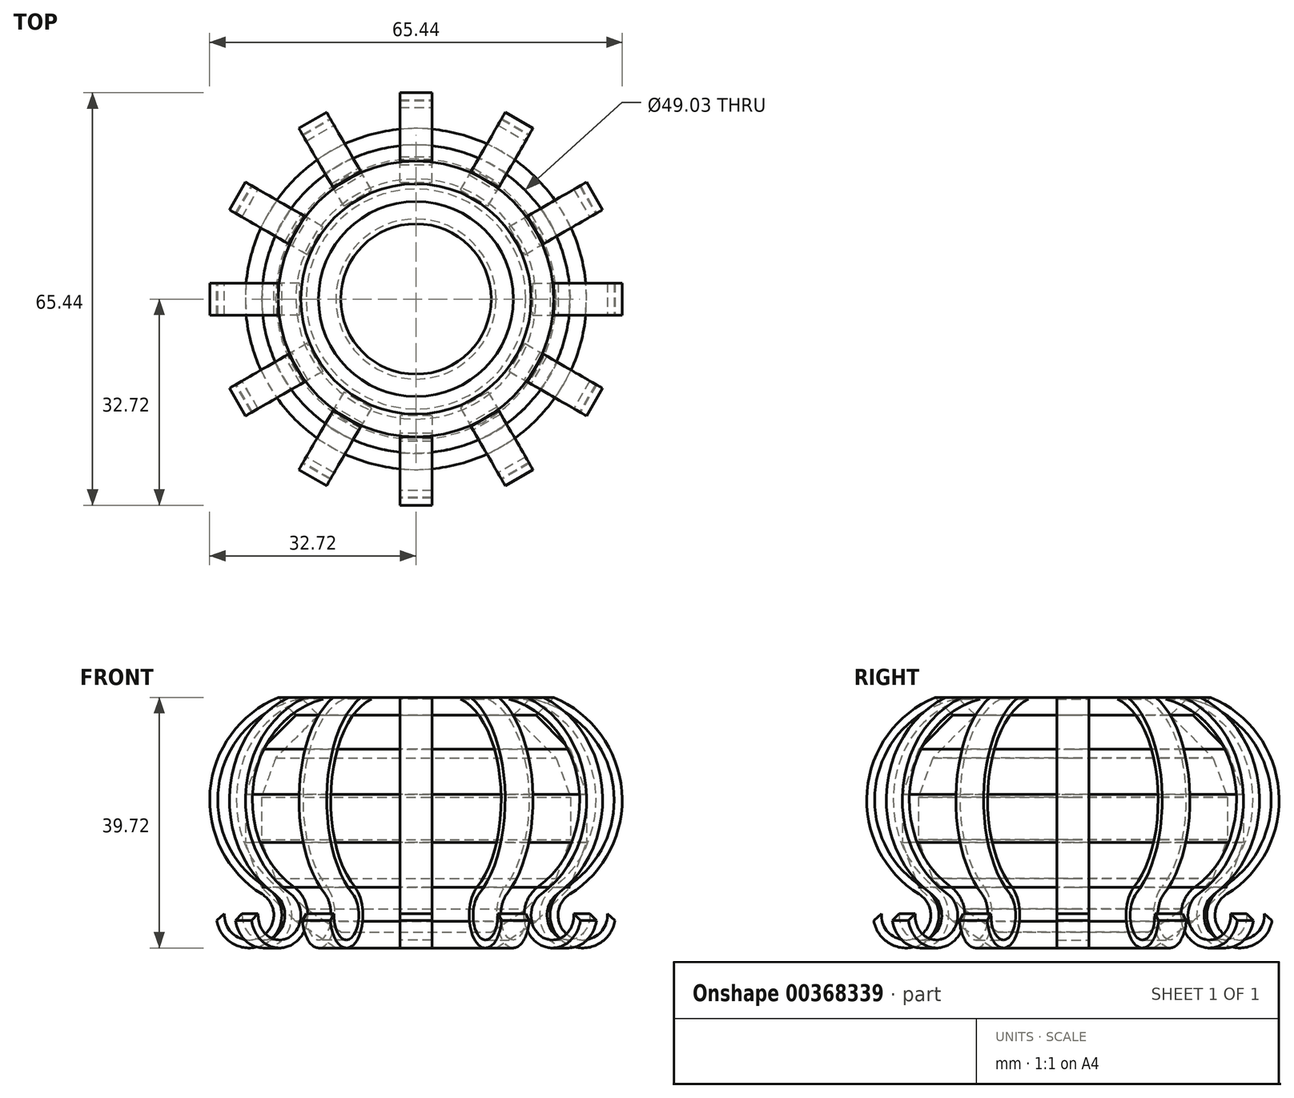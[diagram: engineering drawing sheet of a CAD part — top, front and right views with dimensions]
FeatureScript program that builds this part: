
annotation { "Feature Type Name" : "Feature", "Feature Type Description" : "" }
export const myFeature = defineFeature(function(context is Context, id is Id, definition is map)
    precondition{}
    {
        {
            var Q0;
            Q0=qCreatedBy(makeId("Front.planeOp"),FACE);
            var sketch = newSketch(context, id + "F0", { "sketchPlane" : qUnion([Q0])});
            skLineSegment(sketch, "E0", {"start": v(0, -23.47) * mm, "end": v(-12.7, -23.47) * mm});
            skLineSegment(sketch, "E1", {"start": v(-12.7, -23.47) * mm, "end": v(-19.05, -19.26) * mm});
            skLineSegment(sketch, "E2", {"start": v(-19.05, -19.26) * mm, "end": v(-24.44, -13.87) * mm});
            skLineSegment(sketch, "E3", {"start": v(-24.44, -13.87) * mm, "end": v(-27.06, -6.72) * mm});
            skLineSegment(sketch, "E4", {"start": v(-27.06, -6.72) * mm, "end": v(-27.06, 0.9) * mm});
            skLineSegment(sketch, "E5", {"start": v(-27.06, 0.9) * mm, "end": v(-24.44, 8.06) * mm});
            skLineSegment(sketch, "E6", {"start": v(-24.44, 8.06) * mm, "end": v(-19.05, 13.45) * mm});
            skLineSegment(sketch, "E7", {"start": v(-19.05, 13.45) * mm, "end": v(-21.86, 16.25) * mm});
            skLineSegment(sketch, "E8.0", {"start": v(-15.46, 13.45) * mm, "end": v(-18.27, 16.25) * mm});
            skLineSegment(sketch, "E8.1", {"start": v(-22.25, 6.66) * mm, "end": v(-15.46, 13.45) * mm});
            skLineSegment(sketch, "E8.2", {"start": v(-24.52, 0.45) * mm, "end": v(-22.25, 6.66) * mm});
            skLineSegment(sketch, "E8.3", {"start": v(-24.52, -6.27) * mm, "end": v(-24.52, 0.45) * mm});
            skLineSegment(sketch, "E8.4", {"start": v(0, -20.93) * mm, "end": v(-11.93, -20.93) * mm});
            skLineSegment(sketch, "E8.5", {"start": v(-11.93, -20.93) * mm, "end": v(-17.43, -17.28) * mm});
            skLineSegment(sketch, "E8.6", {"start": v(-17.43, -17.28) * mm, "end": v(-22.25, -12.47) * mm});
            skLineSegment(sketch, "E8.7", {"start": v(-22.25, -12.47) * mm, "end": v(-24.52, -6.27) * mm});
            skLineSegment(sketch, "E9", {"start": v(-21.86, 16.25) * mm, "end": v(-18.27, 16.25) * mm});
            skLineSegment(sketch, "E10", {"start": v(0, -23.47) * mm, "end": v(0, -20.93) * mm});
            skSolve(sketch);
        }
        {
            var Q0;
            Q0 = qSketchRegion(id + "F0", true);
            var Q1;
            Q1=sQuery(id+"F0.wireOp",EDGE,"E10");
            revolve(context, id + "F1", {"entities" : qUnion([Q0]), "axis" : qUnion([Q1]), "revolveType" : RevolveType.FULL});
        }
        {
            var Q0;
            Q0=qCreatedBy(makeId("Front.planeOp"),FACE);
            var sketch = newSketch(context, id + "F2", { "sketchPlane" : qUnion([Q0])});
            skArc(sketch, "E11", {"start": v(-21.86, 16.25) * mm, "mid": v(-32.66, 1.43) * mm, "end": v(-24.4, -14.95) * mm});
            skArc(sketch, "E12", {"start": v(-30.38, -18.03) * mm, "mid": v(-24.67, -21.77) * mm, "end": v(-24.4, -14.95) * mm});
            skLineSegment(sketch, "E13", {"start": v(-29.58, -23.47) * mm, "end": v(-12.7, -23.47) * mm, "construction": true});
            skArc(sketch, "E14.0", {"start": v(-31.59, -19.1) * mm, "mid": v(-23.59, -22.6) * mm, "end": v(-23.73, -13.87) * mm});
            skArc(sketch, "E14.1", {"start": v(-18.5, 15.97) * mm, "mid": v(-31.2, 2.82) * mm, "end": v(-23.73, -13.87) * mm});
            skLineSegment(sketch, "E15", {"start": v(-31.59, -19.1) * mm, "end": v(-30.38, -18.03) * mm});
            skLineSegment(sketch, "E16", {"start": v(-18.5, 15.97) * mm, "end": v(-21.86, 16.25) * mm});
            skSolve(sketch);
        }
        {
            var Q0;
            Q0 = qSketchRegion(id + "F2", true);
            extrude(context, id + "F3", {"entities" : qUnion([Q0]), "endBound" : BoundingType.SYMMETRIC, "depth" : 5.08 * mm});
        }
        {
            var Q0;
            Q0=makeQuery(id+"F3.opExtrude","SWEPT_BODY",BODY,{"disambiguationData":[OSD([sQuery(id+"F2.wireOp",EDGE,"E11"),sQuery(id+"F2.wireOp",EDGE,"E12"),sQuery(id+"F2.wireOp",EDGE,"E14.0"),sQuery(id+"F2.wireOp",EDGE,"E14.1"),sQuery(id+"F2.wireOp",EDGE,"E15"),sQuery(id+"F2.wireOp",EDGE,"E16")])]});
            var Q1;
            Q1=sQuery(id+"F0.wireOp",EDGE,"E10");
            transform(context, id + "F4", {"entities" : qUnion([Q0]), "transformType" : TransformType.ROTATION, "transformAxis" : qUnion([Q1]), "angle" : 30 * degree, "makeCopy" : true});
        }
        {
            var Q0;
            Q0=makeQuery(id+"F4.opPattern","COPY",BODY,{"derivedFrom":makeQuery(id+"F3.opExtrude","SWEPT_BODY",BODY,{"disambiguationData":[OSD([sQuery(id+"F2.wireOp",EDGE,"E11"),sQuery(id+"F2.wireOp",EDGE,"E12"),sQuery(id+"F2.wireOp",EDGE,"E14.0"),sQuery(id+"F2.wireOp",EDGE,"E14.1"),sQuery(id+"F2.wireOp",EDGE,"E15"),sQuery(id+"F2.wireOp",EDGE,"E16")])]}),"instanceName":"1"});
            var Q1;
            Q1=sQuery(id+"F0.wireOp",EDGE,"E10");
            transform(context, id + "F5", {"entities" : qUnion([Q0]), "transformType" : TransformType.ROTATION, "transformAxis" : qUnion([Q1]), "angle" : 30 * degree, "makeCopy" : true});
        }
        {
            var Q0;
            Q0=makeQuery(id+"F5.opPattern","COPY",BODY,{"derivedFrom":makeQuery(id+"F4.opPattern","COPY",BODY,{"derivedFrom":makeQuery(id+"F3.opExtrude","SWEPT_BODY",BODY,{"disambiguationData":[OSD([sQuery(id+"F2.wireOp",EDGE,"E11"),sQuery(id+"F2.wireOp",EDGE,"E12"),sQuery(id+"F2.wireOp",EDGE,"E14.0"),sQuery(id+"F2.wireOp",EDGE,"E14.1"),sQuery(id+"F2.wireOp",EDGE,"E15"),sQuery(id+"F2.wireOp",EDGE,"E16")])]}),"instanceName":"1"}),"instanceName":"1"});
            var Q1;
            Q1=sQuery(id+"F0.wireOp",EDGE,"E10");
            transform(context, id + "F6", {"entities" : qUnion([Q0]), "transformType" : TransformType.ROTATION, "transformAxis" : qUnion([Q1]), "angle" : 30 * degree, "makeCopy" : true});
        }
        {
            var Q0;
            Q0=makeQuery(id+"F6.opPattern","COPY",BODY,{"derivedFrom":makeQuery(id+"F5.opPattern","COPY",BODY,{"derivedFrom":makeQuery(id+"F4.opPattern","COPY",BODY,{"derivedFrom":makeQuery(id+"F3.opExtrude","SWEPT_BODY",BODY,{"disambiguationData":[OSD([sQuery(id+"F2.wireOp",EDGE,"E11"),sQuery(id+"F2.wireOp",EDGE,"E12"),sQuery(id+"F2.wireOp",EDGE,"E14.0"),sQuery(id+"F2.wireOp",EDGE,"E14.1"),sQuery(id+"F2.wireOp",EDGE,"E15"),sQuery(id+"F2.wireOp",EDGE,"E16")])]}),"instanceName":"1"}),"instanceName":"1"}),"instanceName":"1"});
            var Q1;
            Q1=sQuery(id+"F0.wireOp",EDGE,"E10");
            transform(context, id + "F7", {"entities" : qUnion([Q0]), "transformType" : TransformType.ROTATION, "transformAxis" : qUnion([Q1]), "angle" : 30 * degree, "makeCopy" : true});
        }
        {
            var Q0;
            Q0=makeQuery(id+"F7.opPattern","COPY",BODY,{"derivedFrom":makeQuery(id+"F6.opPattern","COPY",BODY,{"derivedFrom":makeQuery(id+"F5.opPattern","COPY",BODY,{"derivedFrom":makeQuery(id+"F4.opPattern","COPY",BODY,{"derivedFrom":makeQuery(id+"F3.opExtrude","SWEPT_BODY",BODY,{"disambiguationData":[OSD([sQuery(id+"F2.wireOp",EDGE,"E11"),sQuery(id+"F2.wireOp",EDGE,"E12"),sQuery(id+"F2.wireOp",EDGE,"E14.0"),sQuery(id+"F2.wireOp",EDGE,"E14.1"),sQuery(id+"F2.wireOp",EDGE,"E15"),sQuery(id+"F2.wireOp",EDGE,"E16")])]}),"instanceName":"1"}),"instanceName":"1"}),"instanceName":"1"}),"instanceName":"1"});
            var Q1;
            Q1=sQuery(id+"F0.wireOp",EDGE,"E10");
            transform(context, id + "F8", {"entities" : qUnion([Q0]), "transformType" : TransformType.ROTATION, "transformAxis" : qUnion([Q1]), "angle" : 30 * degree, "makeCopy" : true});
        }
        {
            var Q0;
            Q0=makeQuery(id+"F8.opPattern","COPY",BODY,{"derivedFrom":makeQuery(id+"F7.opPattern","COPY",BODY,{"derivedFrom":makeQuery(id+"F6.opPattern","COPY",BODY,{"derivedFrom":makeQuery(id+"F5.opPattern","COPY",BODY,{"derivedFrom":makeQuery(id+"F4.opPattern","COPY",BODY,{"derivedFrom":makeQuery(id+"F3.opExtrude","SWEPT_BODY",BODY,{"disambiguationData":[OSD([sQuery(id+"F2.wireOp",EDGE,"E11"),sQuery(id+"F2.wireOp",EDGE,"E12"),sQuery(id+"F2.wireOp",EDGE,"E14.0"),sQuery(id+"F2.wireOp",EDGE,"E14.1"),sQuery(id+"F2.wireOp",EDGE,"E15"),sQuery(id+"F2.wireOp",EDGE,"E16")])]}),"instanceName":"1"}),"instanceName":"1"}),"instanceName":"1"}),"instanceName":"1"}),"instanceName":"1"});
            var Q1;
            Q1=sQuery(id+"F0.wireOp",EDGE,"E10");
            transform(context, id + "F9", {"entities" : qUnion([Q0]), "transformType" : TransformType.ROTATION, "transformAxis" : qUnion([Q1]), "angle" : 30 * degree, "makeCopy" : true});
        }
        {
            var Q0;
            Q0=makeQuery(id+"F9.opPattern","COPY",BODY,{"derivedFrom":makeQuery(id+"F8.opPattern","COPY",BODY,{"derivedFrom":makeQuery(id+"F7.opPattern","COPY",BODY,{"derivedFrom":makeQuery(id+"F6.opPattern","COPY",BODY,{"derivedFrom":makeQuery(id+"F5.opPattern","COPY",BODY,{"derivedFrom":makeQuery(id+"F4.opPattern","COPY",BODY,{"derivedFrom":makeQuery(id+"F3.opExtrude","SWEPT_BODY",BODY,{"disambiguationData":[OSD([sQuery(id+"F2.wireOp",EDGE,"E11"),sQuery(id+"F2.wireOp",EDGE,"E12"),sQuery(id+"F2.wireOp",EDGE,"E14.0"),sQuery(id+"F2.wireOp",EDGE,"E14.1"),sQuery(id+"F2.wireOp",EDGE,"E15"),sQuery(id+"F2.wireOp",EDGE,"E16")])]}),"instanceName":"1"}),"instanceName":"1"}),"instanceName":"1"}),"instanceName":"1"}),"instanceName":"1"}),"instanceName":"1"});
            var Q1;
            Q1=sQuery(id+"F0.wireOp",EDGE,"E10");
            transform(context, id + "F10", {"entities" : qUnion([Q0]), "transformType" : TransformType.ROTATION, "transformAxis" : qUnion([Q1]), "angle" : 30 * degree, "makeCopy" : true});
        }
        {
            var Q0;
            Q0=makeQuery(id+"F10.opPattern","COPY",BODY,{"derivedFrom":makeQuery(id+"F9.opPattern","COPY",BODY,{"derivedFrom":makeQuery(id+"F8.opPattern","COPY",BODY,{"derivedFrom":makeQuery(id+"F7.opPattern","COPY",BODY,{"derivedFrom":makeQuery(id+"F6.opPattern","COPY",BODY,{"derivedFrom":makeQuery(id+"F5.opPattern","COPY",BODY,{"derivedFrom":makeQuery(id+"F4.opPattern","COPY",BODY,{"derivedFrom":makeQuery(id+"F3.opExtrude","SWEPT_BODY",BODY,{"disambiguationData":[OSD([sQuery(id+"F2.wireOp",EDGE,"E11"),sQuery(id+"F2.wireOp",EDGE,"E12"),sQuery(id+"F2.wireOp",EDGE,"E14.0"),sQuery(id+"F2.wireOp",EDGE,"E14.1"),sQuery(id+"F2.wireOp",EDGE,"E15"),sQuery(id+"F2.wireOp",EDGE,"E16")])]}),"instanceName":"1"}),"instanceName":"1"}),"instanceName":"1"}),"instanceName":"1"}),"instanceName":"1"}),"instanceName":"1"}),"instanceName":"1"});
            var Q1;
            Q1=sQuery(id+"F0.wireOp",EDGE,"E10");
            transform(context, id + "F11", {"entities" : qUnion([Q0]), "transformType" : TransformType.ROTATION, "transformAxis" : qUnion([Q1]), "angle" : 30 * degree, "makeCopy" : true});
        }
        {
            var Q0;
            Q0=makeQuery(id+"F11.opPattern","COPY",BODY,{"derivedFrom":makeQuery(id+"F10.opPattern","COPY",BODY,{"derivedFrom":makeQuery(id+"F9.opPattern","COPY",BODY,{"derivedFrom":makeQuery(id+"F8.opPattern","COPY",BODY,{"derivedFrom":makeQuery(id+"F7.opPattern","COPY",BODY,{"derivedFrom":makeQuery(id+"F6.opPattern","COPY",BODY,{"derivedFrom":makeQuery(id+"F5.opPattern","COPY",BODY,{"derivedFrom":makeQuery(id+"F4.opPattern","COPY",BODY,{"derivedFrom":makeQuery(id+"F3.opExtrude","SWEPT_BODY",BODY,{"disambiguationData":[OSD([sQuery(id+"F2.wireOp",EDGE,"E11"),sQuery(id+"F2.wireOp",EDGE,"E12"),sQuery(id+"F2.wireOp",EDGE,"E14.0"),sQuery(id+"F2.wireOp",EDGE,"E14.1"),sQuery(id+"F2.wireOp",EDGE,"E15"),sQuery(id+"F2.wireOp",EDGE,"E16")])]}),"instanceName":"1"}),"instanceName":"1"}),"instanceName":"1"}),"instanceName":"1"}),"instanceName":"1"}),"instanceName":"1"}),"instanceName":"1"}),"instanceName":"1"});
            var Q1;
            Q1=sQuery(id+"F0.wireOp",EDGE,"E10");
            transform(context, id + "F12", {"entities" : qUnion([Q0]), "transformType" : TransformType.ROTATION, "transformAxis" : qUnion([Q1]), "angle" : 30 * degree, "makeCopy" : true});
        }
        {
            var Q0;
            Q0=makeQuery(id+"F12.opPattern","COPY",BODY,{"derivedFrom":makeQuery(id+"F11.opPattern","COPY",BODY,{"derivedFrom":makeQuery(id+"F10.opPattern","COPY",BODY,{"derivedFrom":makeQuery(id+"F9.opPattern","COPY",BODY,{"derivedFrom":makeQuery(id+"F8.opPattern","COPY",BODY,{"derivedFrom":makeQuery(id+"F7.opPattern","COPY",BODY,{"derivedFrom":makeQuery(id+"F6.opPattern","COPY",BODY,{"derivedFrom":makeQuery(id+"F5.opPattern","COPY",BODY,{"derivedFrom":makeQuery(id+"F4.opPattern","COPY",BODY,{"derivedFrom":makeQuery(id+"F3.opExtrude","SWEPT_BODY",BODY,{"disambiguationData":[OSD([sQuery(id+"F2.wireOp",EDGE,"E11"),sQuery(id+"F2.wireOp",EDGE,"E12"),sQuery(id+"F2.wireOp",EDGE,"E14.0"),sQuery(id+"F2.wireOp",EDGE,"E14.1"),sQuery(id+"F2.wireOp",EDGE,"E15"),sQuery(id+"F2.wireOp",EDGE,"E16")])]}),"instanceName":"1"}),"instanceName":"1"}),"instanceName":"1"}),"instanceName":"1"}),"instanceName":"1"}),"instanceName":"1"}),"instanceName":"1"}),"instanceName":"1"}),"instanceName":"1"});
            var Q1;
            Q1=sQuery(id+"F0.wireOp",EDGE,"E10");
            transform(context, id + "F13", {"entities" : qUnion([Q0]), "transformType" : TransformType.ROTATION, "transformAxis" : qUnion([Q1]), "angle" : 30 * degree, "makeCopy" : true});
        }
        {
            var Q0;
            Q0=makeQuery(id+"F13.opPattern","COPY",BODY,{"derivedFrom":makeQuery(id+"F12.opPattern","COPY",BODY,{"derivedFrom":makeQuery(id+"F11.opPattern","COPY",BODY,{"derivedFrom":makeQuery(id+"F10.opPattern","COPY",BODY,{"derivedFrom":makeQuery(id+"F9.opPattern","COPY",BODY,{"derivedFrom":makeQuery(id+"F8.opPattern","COPY",BODY,{"derivedFrom":makeQuery(id+"F7.opPattern","COPY",BODY,{"derivedFrom":makeQuery(id+"F6.opPattern","COPY",BODY,{"derivedFrom":makeQuery(id+"F5.opPattern","COPY",BODY,{"derivedFrom":makeQuery(id+"F4.opPattern","COPY",BODY,{"derivedFrom":makeQuery(id+"F3.opExtrude","SWEPT_BODY",BODY,{"disambiguationData":[OSD([sQuery(id+"F2.wireOp",EDGE,"E11"),sQuery(id+"F2.wireOp",EDGE,"E12"),sQuery(id+"F2.wireOp",EDGE,"E14.0"),sQuery(id+"F2.wireOp",EDGE,"E14.1"),sQuery(id+"F2.wireOp",EDGE,"E15"),sQuery(id+"F2.wireOp",EDGE,"E16")])]}),"instanceName":"1"}),"instanceName":"1"}),"instanceName":"1"}),"instanceName":"1"}),"instanceName":"1"}),"instanceName":"1"}),"instanceName":"1"}),"instanceName":"1"}),"instanceName":"1"}),"instanceName":"1"});
            var Q1;
            Q1=sQuery(id+"F0.wireOp",EDGE,"E10");
            transform(context, id + "F14", {"entities" : qUnion([Q0]), "transformType" : TransformType.ROTATION, "transformAxis" : qUnion([Q1]), "angle" : 30 * degree, "makeCopy" : true});
        }
    });
